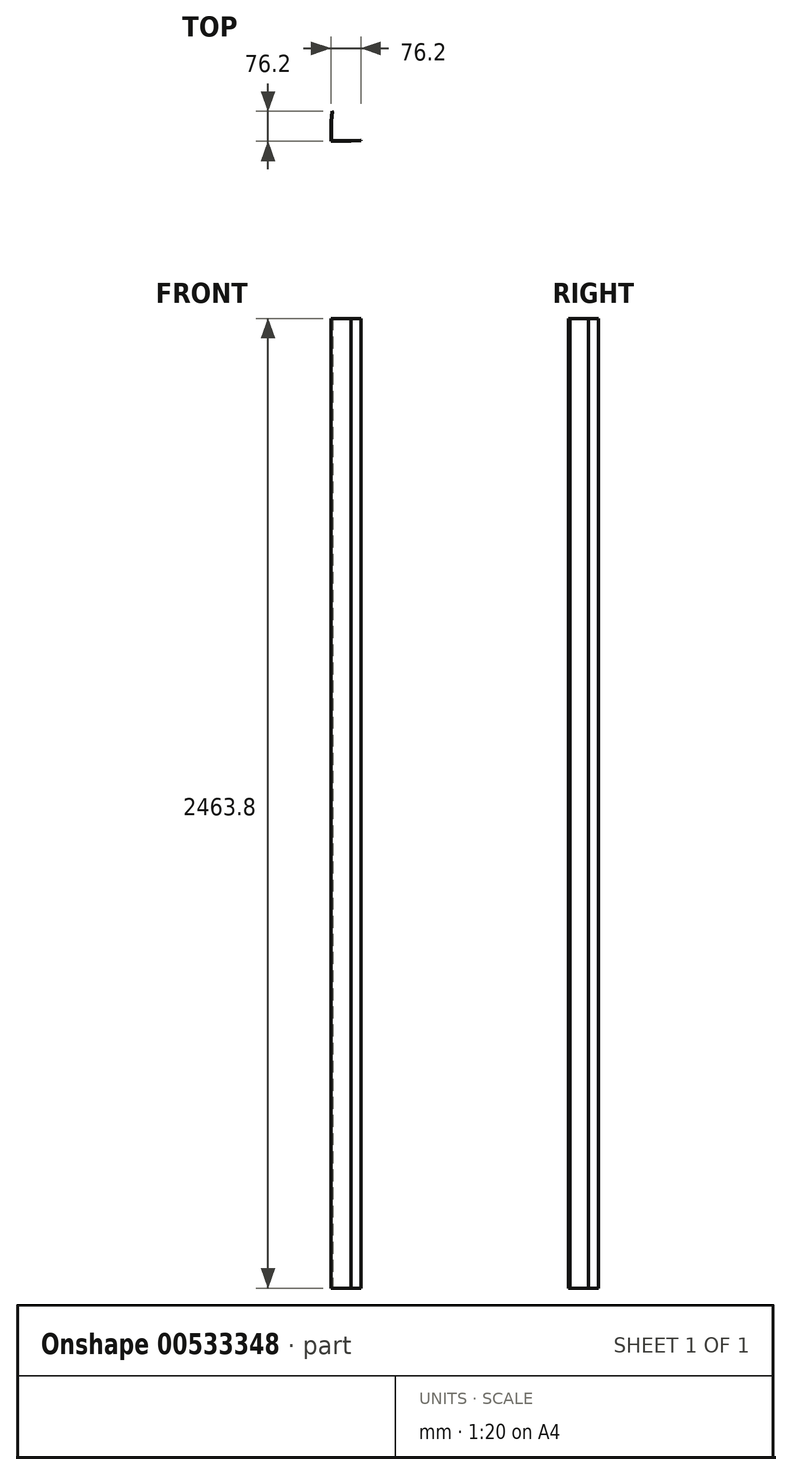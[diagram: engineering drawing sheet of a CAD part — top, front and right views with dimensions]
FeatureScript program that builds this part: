
annotation { "Feature Type Name" : "Feature", "Feature Type Description" : "" }
export const myFeature = defineFeature(function(context is Context, id is Id, definition is map)
    precondition{}
    {
        {
            var Q0;
            Q0=qCreatedBy(makeId("Top.planeOp"),FACE);
            var sketch = newSketch(context, id + "F0", { "sketchPlane" : qUnion([Q0])});
            skLineSegment(sketch, "E0", {"start": v(2.21, 76.2) * mm, "end": v(0, 50.9) * mm});
            skLineSegment(sketch, "E1", {"start": v(0, 50.9) * mm, "end": v(0, 0) * mm});
            skLineSegment(sketch, "E2", {"start": v(0, 0) * mm, "end": v(23.28, 23.28) * mm, "construction": true});
            skLineSegment(sketch, "E3.0", {"start": v(1.27, 50.84) * mm, "end": v(1.27, 1.27) * mm});
            skLineSegment(sketch, "E3.1", {"start": v(3.48, 76.09) * mm, "end": v(1.27, 50.84) * mm});
            skLineSegment(sketch, "E4", {"start": v(3.48, 76.09) * mm, "end": v(2.21, 76.2) * mm});
            skLineSegment(sketch, "E5.MirrorCS", {"start": v(76.09, 3.48) * mm, "end": v(76.2, 2.21) * mm});
            skLineSegment(sketch, "E6.MirrorCS", {"start": v(76.2, 2.21) * mm, "end": v(50.9, 0) * mm});
            skLineSegment(sketch, "E7.MirrorCS", {"start": v(50.9, 0) * mm, "end": v(0, 0) * mm});
            skLineSegment(sketch, "E8.MirrorCS", {"start": v(76.09, 3.48) * mm, "end": v(50.84, 1.27) * mm});
            skLineSegment(sketch, "E9.MirrorCS", {"start": v(50.84, 1.27) * mm, "end": v(1.27, 1.27) * mm});
            skSolve(sketch);
        }
        {
            var Q0;
            Q0 = qSketchRegion(id + "F0", true);
            extrude(context, id + "F1", {"entities" : qUnion([Q0]), "depth" : 2463.8 * mm, "offsetDistance" : 25.4 * mm});
        }
    });
